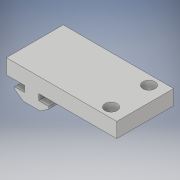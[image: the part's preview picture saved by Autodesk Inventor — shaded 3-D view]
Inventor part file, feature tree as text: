
AUTODESK INVENTOR PART (.ipt)
format: ipt  version: 2017 (Build 210142000, 142)  size: 146,944 bytes
history: native  units: in
note: dims shown in document units (in); Inventor stores cm internally (conversion verified against a paired STEP export)
features: sketch x3, extrude x2, hole x1
ambient origin geometry x8: Origin, YZ Plane, XZ Plane, XY Plane, X Axis, Y Axis, Z Axis, Center Point
bodies: Solid1 (feature_tree)
feature tree (6):
  extrude  "Extrusion1"  Depth=0.0787in
  extrude  "Extrusion2"  Depth=0.4524in
  hole  "Hole1"  [1 undecoded]
  sketch  "Sketch1"  dims[d0=0.6693in d2=0.1969in d3=0.0787in]
  sketch  "Sketch2"  dims[d4=0.1874in d6=0.4524in]
  sketch  "Sketch3"  dims[d7=0.1085in d8=0.225in d9=0.2221in d10=0.2409in d11=0.03in d12=0.03in d13=0.75in d14=0.0in d16=1.0268in d19=0.5018in d20=0.5018in d21=0.2838in d22=0.2838in d23=0.1181in d24=0.1181in d25=0.1181in d26=0.0in d27=0.2in d28=0.2in d29=0.16in d30=0.75in d31=0.375in d32=0.25in d33=0.5635in d34=1.0in d35=0.8108in d36=0.125in d37=0.125in d50=0.9949in d51=0.1137in]
note: 1 required parameter value undecoded (feature->parameter linkage not recoverable at this tier; creation-order binding heuristic only, values carry confidence <= 0.55)
